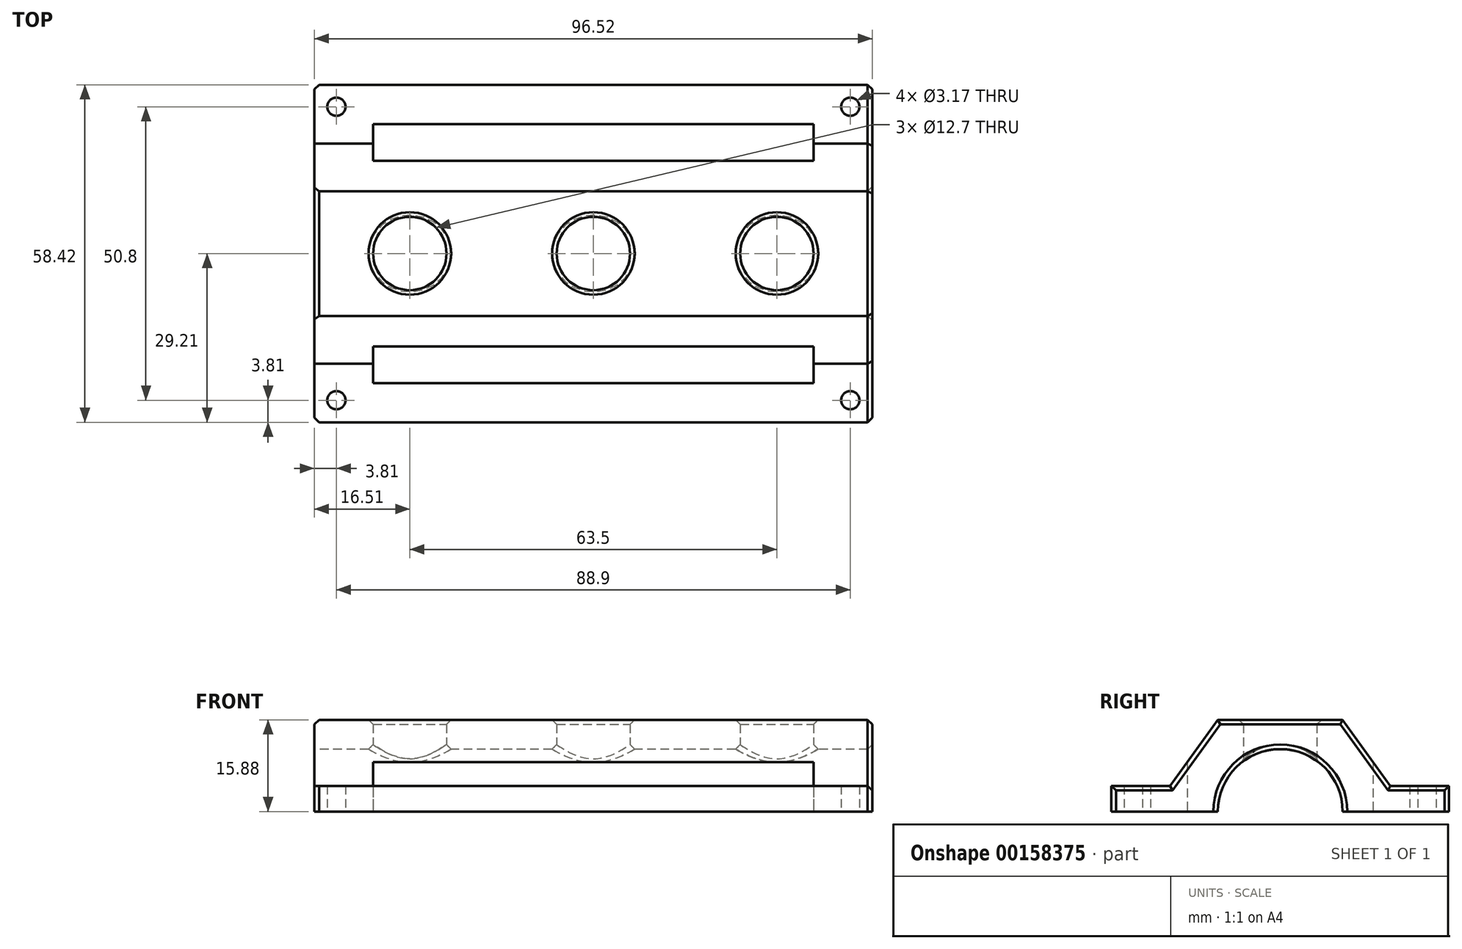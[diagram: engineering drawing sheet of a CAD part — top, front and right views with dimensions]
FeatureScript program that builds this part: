
annotation { "Feature Type Name" : "Feature", "Feature Type Description" : "" }
export const myFeature = defineFeature(function(context is Context, id is Id, definition is map)
    precondition{}
    {
        {
            var Q0;
            Q0=qCreatedBy(makeId("Top.planeOp"),FACE);
            var sketch = newSketch(context, id + "F0", { "sketchPlane" : qUnion([Q0])});
            skLineSegment(sketch, "E0", {"start": v(0, 0) * mm, "end": v(-48.26, 0) * mm});
            skLineSegment(sketch, "E1", {"start": v(-48.26, 0) * mm, "end": v(-48.26, 29.21) * mm});
            skLineSegment(sketch, "E2", {"start": v(-48.26, 29.21) * mm, "end": v(0, 29.21) * mm});
            skLineSegment(sketch, "E3", {"start": v(0, 29.21) * mm, "end": v(0, 0) * mm});
            skLineSegment(sketch, "E4.MirrorCS", {"start": v(48.26, 29.21) * mm, "end": v(0, 29.21) * mm});
            skLineSegment(sketch, "E5.MirrorCS", {"start": v(48.26, 0) * mm, "end": v(48.26, 29.21) * mm});
            skLineSegment(sketch, "E6.MirrorCS", {"start": v(0, 0) * mm, "end": v(48.26, 0) * mm});
            skLineSegment(sketch, "E7.MirrorCS", {"start": v(-48.26, -29.21) * mm, "end": v(0, -29.21) * mm});
            skLineSegment(sketch, "E8.MirrorCS", {"start": v(48.26, -29.2) * mm, "end": v(0, -29.21) * mm});
            skLineSegment(sketch, "E9.MirrorCS", {"start": v(48.26, 0) * mm, "end": v(48.26, -29.21) * mm});
            skLineSegment(sketch, "E10.MirrorCS", {"start": v(-48.26, 0) * mm, "end": v(-48.26, -29.21) * mm});
            skSolve(sketch);
        }
        {
            var Q0;
            Q0 = qSketchRegion(id + "F0", true);
            var Q1;
            Q1 = qSketchRegion(id + "F1MxHlLQY0lKD1c_1", true);
            extrude(context, id + "F1", {"entities" : qUnion([Q0, Q1]), "depth" : 15.88 * mm});
        }
        {
            var Q0;
            Q0=makeQuery(id+"F1.opExtrude","SWEPT_FACE",FACE,{"disambiguationData":[OSD([sQuery(id+"F0.wireOp",EDGE,"E1"),sQuery(id+"F0.wireOp",EDGE,"E10.MirrorCS")])]});
            var sketch = newSketch(context, id + "F2", { "sketchPlane" : qUnion([Q0])});
            skCircle(sketch, "E11", {"center": v(0, 0) * mm, "radius": 10.8 * mm});
            skLineSegment(sketch, "E12", {"start": v(-29.21, 15.88) * mm, "end": v(-10.8, 15.88) * mm});
            skLineSegment(sketch, "E13", {"start": v(-10.8, 15.88) * mm, "end": v(-19.05, 4.45) * mm});
            skLineSegment(sketch, "E14", {"start": v(-19.05, 4.45) * mm, "end": v(-29.21, 4.44) * mm});
            skLineSegment(sketch, "E15", {"start": v(-29.21, 4.44) * mm, "end": v(-29.21, 15.88) * mm});
            skLineSegment(sketch, "E16.MirrorCS", {"start": v(10.8, 15.88) * mm, "end": v(19.05, 4.44) * mm});
            skLineSegment(sketch, "E17.MirrorCS", {"start": v(19.05, 4.45) * mm, "end": v(29.21, 4.44) * mm});
            skLineSegment(sketch, "E18.MirrorCS", {"start": v(29.21, 4.44) * mm, "end": v(29.21, 15.88) * mm});
            skLineSegment(sketch, "E19.MirrorCS", {"start": v(29.21, 15.88) * mm, "end": v(10.8, 15.88) * mm});
            skSolve(sketch);
        }
        {
            var Q0;
            Q0 = qSketchRegion(id + "F2", true);
            extrude(context, id + "F3", {"entities" : qUnion([Q0]), "operationType" : NewBodyOperationType.REMOVE, "oppositeDirection" : true, "depth" : 101.6 * mm});
        }
        {
            var Q0;
            Q0=qCreatedBy(makeId("Top.planeOp"),FACE);
            var sketch = newSketch(context, id + "F4", { "sketchPlane" : qUnion([Q0])});
            skCircle(sketch, "E20", {"center": v(-44.45, 25.4) * mm, "radius": 1.59 * mm});
            skCircle(sketch, "E21.MirrorC", {"center": v(44.45, 25.4) * mm, "radius": 1.59 * mm});
            skCircle(sketch, "E22.MirrorC", {"center": v(44.45, -25.4) * mm, "radius": 1.59 * mm});
            skCircle(sketch, "E23.MirrorC", {"center": v(-44.45, -25.4) * mm, "radius": 1.59 * mm});
            skLineSegment(sketch, "E24.bottom", {"start": v(-38.1, 22.42) * mm, "end": v(38.1, 22.42) * mm});
            skLineSegment(sketch, "E24.top", {"start": v(-38.1, 16.07) * mm, "end": v(38.1, 16.07) * mm});
            skLineSegment(sketch, "E24.left", {"start": v(-38.1, 22.42) * mm, "end": v(-38.1, 16.07) * mm});
            skLineSegment(sketch, "E24.right", {"start": v(38.1, 22.42) * mm, "end": v(38.1, 16.07) * mm});
            skLineSegment(sketch, "E25.MirrorCS", {"start": v(-38.1, -16.07) * mm, "end": v(38.1, -16.07) * mm});
            skLineSegment(sketch, "E26.MirrorCS", {"start": v(-38.1, -22.42) * mm, "end": v(-38.1, -16.07) * mm});
            skLineSegment(sketch, "E27.MirrorCS", {"start": v(-38.1, -22.42) * mm, "end": v(38.1, -22.42) * mm});
            skLineSegment(sketch, "E28.MirrorCS", {"start": v(38.1, -22.42) * mm, "end": v(38.1, -16.07) * mm});
            skCircle(sketch, "E29", {"center": v(-31.75, 0) * mm, "radius": 6.35 * mm});
            skCircle(sketch, "E30", {"center": v(0, 0) * mm, "radius": 6.35 * mm});
            skCircle(sketch, "E31.MirrorC", {"center": v(31.75, 0) * mm, "radius": 6.35 * mm});
            skSolve(sketch);
        }
        {
            var Q0;
            Q0 = qSketchRegion(id + "F4", true);
            extrude(context, id + "F5", {"entities" : qUnion([Q0]), "operationType" : NewBodyOperationType.REMOVE, "depth" : 25.4 * mm});
        }
        {
            var Q0;
            Q0=makeQuery(id+"F5.boolean.opBoolean","COPY",EDGE,{"derivedFrom":makeQuery(id+"F5.opExtrude","CAP_EDGE",EDGE,{"disambiguationData":[OSD([sQuery(id+"F4.wireOp",EDGE,"E24.bottom")])],"isStart":true})});
            var Q1;
            Q1=makeQuery(id+"F5.boolean.opBoolean","COPY",EDGE,{"derivedFrom":makeQuery(id+"F5.opExtrude","CAP_EDGE",EDGE,{"disambiguationData":[OSD([sQuery(id+"F4.wireOp",EDGE,"E24.top")])],"isStart":true})});
            var Q2;
            Q2=makeQuery(id+"F5.boolean.opBoolean","COPY",EDGE,{"derivedFrom":makeQuery(id+"F5.opExtrude","CAP_EDGE",EDGE,{"disambiguationData":[OSD([sQuery(id+"F4.wireOp",EDGE,"E24.left")])],"isStart":true})});
            var Q3;
            Q3=makeQuery(id+"F5.boolean.opBoolean","COPY",EDGE,{"derivedFrom":makeQuery(id+"F5.opExtrude","CAP_EDGE",EDGE,{"disambiguationData":[OSD([sQuery(id+"F4.wireOp",EDGE,"E24.right")])],"isStart":true})});
            var Q4;
            Q4=makeQuery(id+"F5.boolean.opBoolean","COPY",EDGE,{"derivedFrom":makeQuery(id+"F5.opExtrude","CAP_EDGE",EDGE,{"disambiguationData":[OSD([sQuery(id+"F4.wireOp",EDGE,"E25.MirrorCS")])],"isStart":true})});
            var Q5;
            Q5=makeQuery(id+"F5.boolean.opBoolean","COPY",EDGE,{"derivedFrom":makeQuery(id+"F5.opExtrude","CAP_EDGE",EDGE,{"disambiguationData":[OSD([sQuery(id+"F4.wireOp",EDGE,"E27.MirrorCS")])],"isStart":true})});
            var Q6;
            Q6=makeQuery(id+"F5.boolean.opBoolean","COPY",EDGE,{"derivedFrom":makeQuery(id+"F5.opExtrude","CAP_EDGE",EDGE,{"disambiguationData":[OSD([sQuery(id+"F4.wireOp",EDGE,"E28.MirrorCS")])],"isStart":true})});
            var Q7;
            Q7=makeQuery(id+"F5.boolean.opBoolean","COPY",EDGE,{"derivedFrom":makeQuery(id+"F5.opExtrude","CAP_EDGE",EDGE,{"disambiguationData":[OSD([sQuery(id+"F4.wireOp",EDGE,"E26.MirrorCS")])],"isStart":true})});
            var Q8;
            Q8=makeQuery(id+"F5.boolean.opBoolean","INTERSECT",EDGE,{"derivedFrom":[makeQuery(id+"F3.boolean.opBoolean","COPY",FACE,{"derivedFrom":makeQuery(id+"F3.opExtrude","SWEPT_FACE",FACE,{"disambiguationData":[OSD([sQuery(id+"F2.wireOp",EDGE,"E11")])]})}),makeQuery(id+"F5.opExtrude","SWEPT_FACE",FACE,{"disambiguationData":[OSD([sQuery(id+"F4.wireOp",EDGE,"E29")])]})]});
            var Q9;
            Q9=makeQuery(id+"F5.boolean.opBoolean","INTERSECT",EDGE,{"derivedFrom":[makeQuery(id+"F3.boolean.opBoolean","COPY",FACE,{"derivedFrom":makeQuery(id+"F3.opExtrude","SWEPT_FACE",FACE,{"disambiguationData":[OSD([sQuery(id+"F2.wireOp",EDGE,"E11")])]})}),makeQuery(id+"F5.opExtrude","SWEPT_FACE",FACE,{"disambiguationData":[OSD([sQuery(id+"F4.wireOp",EDGE,"E30")])]})]});
            var Q10;
            Q10=makeQuery(id+"F5.boolean.opBoolean","INTERSECT",EDGE,{"derivedFrom":[makeQuery(id+"F3.boolean.opBoolean","COPY",FACE,{"derivedFrom":makeQuery(id+"F3.opExtrude","SWEPT_FACE",FACE,{"disambiguationData":[OSD([sQuery(id+"F2.wireOp",EDGE,"E11")])]})}),makeQuery(id+"F5.opExtrude","SWEPT_FACE",FACE,{"disambiguationData":[OSD([sQuery(id+"F4.wireOp",EDGE,"E31.MirrorC")])]})]});
            var Q11;
            Q11=makeQuery(id+"F5.boolean.opBoolean","INTERSECT",EDGE,{"derivedFrom":[makeQuery(id+"F1.opExtrude","CAP_FACE",FACE,{"disambiguationData":[OSD([sQuery(id+"F0.wireOp",EDGE,"E1"),sQuery(id+"F0.wireOp",EDGE,"E2"),sQuery(id+"F0.wireOp",EDGE,"E4.MirrorCS"),sQuery(id+"F0.wireOp",EDGE,"E5.MirrorCS"),sQuery(id+"F0.wireOp",EDGE,"E7.MirrorCS"),sQuery(id+"F0.wireOp",EDGE,"E8.MirrorCS"),sQuery(id+"F0.wireOp",EDGE,"E9.MirrorCS"),sQuery(id+"F0.wireOp",EDGE,"E10.MirrorCS")])],"isStart":false}),makeQuery(id+"F5.opExtrude","SWEPT_FACE",FACE,{"disambiguationData":[OSD([sQuery(id+"F4.wireOp",EDGE,"E31.MirrorC")])]})]});
            var Q12;
            Q12=makeQuery(id+"F5.boolean.opBoolean","INTERSECT",EDGE,{"derivedFrom":[makeQuery(id+"F1.opExtrude","CAP_FACE",FACE,{"disambiguationData":[OSD([sQuery(id+"F0.wireOp",EDGE,"E1"),sQuery(id+"F0.wireOp",EDGE,"E2"),sQuery(id+"F0.wireOp",EDGE,"E4.MirrorCS"),sQuery(id+"F0.wireOp",EDGE,"E5.MirrorCS"),sQuery(id+"F0.wireOp",EDGE,"E7.MirrorCS"),sQuery(id+"F0.wireOp",EDGE,"E8.MirrorCS"),sQuery(id+"F0.wireOp",EDGE,"E9.MirrorCS"),sQuery(id+"F0.wireOp",EDGE,"E10.MirrorCS")])],"isStart":false}),makeQuery(id+"F5.opExtrude","SWEPT_FACE",FACE,{"disambiguationData":[OSD([sQuery(id+"F4.wireOp",EDGE,"E30")])]})]});
            var Q13;
            Q13=makeQuery(id+"F5.boolean.opBoolean","INTERSECT",EDGE,{"derivedFrom":[makeQuery(id+"F1.opExtrude","CAP_FACE",FACE,{"disambiguationData":[OSD([sQuery(id+"F0.wireOp",EDGE,"E1"),sQuery(id+"F0.wireOp",EDGE,"E2"),sQuery(id+"F0.wireOp",EDGE,"E4.MirrorCS"),sQuery(id+"F0.wireOp",EDGE,"E5.MirrorCS"),sQuery(id+"F0.wireOp",EDGE,"E7.MirrorCS"),sQuery(id+"F0.wireOp",EDGE,"E8.MirrorCS"),sQuery(id+"F0.wireOp",EDGE,"E9.MirrorCS"),sQuery(id+"F0.wireOp",EDGE,"E10.MirrorCS")])],"isStart":false}),makeQuery(id+"F5.opExtrude","SWEPT_FACE",FACE,{"disambiguationData":[OSD([sQuery(id+"F4.wireOp",EDGE,"E29")])]})]});
            var Q14;
            Q14=makeQuery(id+"F3.boolean.opBoolean","INTERSECT",EDGE,{"derivedFrom":[makeQuery(id+"F1.opExtrude","SWEPT_FACE",FACE,{"disambiguationData":[OSD([sQuery(id+"F0.wireOp",EDGE,"E5.MirrorCS"),sQuery(id+"F0.wireOp",EDGE,"E9.MirrorCS")])]}),makeQuery(id+"F3.opExtrude","SWEPT_FACE",FACE,{"disambiguationData":[OSD([sQuery(id+"F2.wireOp",EDGE,"E11")])]})]});
            var Q15;
            Q15=makeQuery(id+"F3.boolean.opBoolean","COPY",EDGE,{"derivedFrom":makeQuery(id+"F3.opExtrude","CAP_EDGE",EDGE,{"disambiguationData":[OSD([sQuery(id+"F2.wireOp",EDGE,"E11")])],"isStart":true})});
            var Q16;
            Q16=makeQuery(id+"F3.boolean.opBoolean","COPY",EDGE,{"derivedFrom":makeQuery(id+"F3.opExtrude","CAP_EDGE",EDGE,{"disambiguationData":[OSD([sQuery(id+"F2.wireOp",EDGE,"E16.MirrorCS")])],"isStart":true})});
            var Q17;
            Q17=makeQuery(id+"F3.boolean.opBoolean","COPY",EDGE,{"derivedFrom":makeQuery(id+"F3.opExtrude","CAP_EDGE",EDGE,{"disambiguationData":[OSD([sQuery(id+"F2.wireOp",EDGE,"E17.MirrorCS")])],"isStart":true})});
            var Q18;
            Q18=makeQuery(id+"F1.opExtrude","CAP_EDGE",EDGE,{"disambiguationData":[OSD([sQuery(id+"F0.wireOp",EDGE,"E1"),sQuery(id+"F0.wireOp",EDGE,"E10.MirrorCS")])],"isStart":false});
            var Q19;
            Q19=makeQuery(id+"F3.boolean.opBoolean","COPY",EDGE,{"derivedFrom":makeQuery(id+"F3.opExtrude","CAP_EDGE",EDGE,{"disambiguationData":[OSD([sQuery(id+"F2.wireOp",EDGE,"E13")])],"isStart":true})});
            var Q20;
            Q20=makeQuery(id+"F3.boolean.opBoolean","COPY",EDGE,{"derivedFrom":makeQuery(id+"F3.opExtrude","CAP_EDGE",EDGE,{"disambiguationData":[OSD([sQuery(id+"F2.wireOp",EDGE,"E14")])],"isStart":true})});
            var Q21;
            Q21=makeQuery(id+"F3.boolean.opBoolean","COPY",EDGE,{"derivedFrom":makeQuery(id+"F3.opExtrude","SWEPT_EDGE",EDGE,{"disambiguationData":[OSD([sQuery(id+"F0.wireOp",EDGE,"E1"),sQuery(id+"F0.wireOp",EDGE,"E2"),sQuery(id+"F2.wireOp",EDGE,"E14"),sQuery(id+"F2.wireOp",EDGE,"E15")])]})});
            var Q22;
            Q22=makeQuery(id+"F3.boolean.opBoolean","INTERSECT",EDGE,{"derivedFrom":[makeQuery(id+"F1.opExtrude","SWEPT_FACE",FACE,{"disambiguationData":[OSD([sQuery(id+"F0.wireOp",EDGE,"E5.MirrorCS"),sQuery(id+"F0.wireOp",EDGE,"E9.MirrorCS")])]}),makeQuery(id+"F3.opExtrude","SWEPT_FACE",FACE,{"disambiguationData":[OSD([sQuery(id+"F2.wireOp",EDGE,"E14")])]})]});
            var Q23;
            Q23=makeQuery(id+"F1.opExtrude","CAP_EDGE",EDGE,{"disambiguationData":[OSD([sQuery(id+"F0.wireOp",EDGE,"E5.MirrorCS"),sQuery(id+"F0.wireOp",EDGE,"E9.MirrorCS")])],"isStart":false});
            var Q24;
            Q24=makeQuery(id+"F3.boolean.opBoolean","INTERSECT",EDGE,{"derivedFrom":[makeQuery(id+"F1.opExtrude","SWEPT_FACE",FACE,{"disambiguationData":[OSD([sQuery(id+"F0.wireOp",EDGE,"E5.MirrorCS"),sQuery(id+"F0.wireOp",EDGE,"E9.MirrorCS")])]}),makeQuery(id+"F3.opExtrude","SWEPT_FACE",FACE,{"disambiguationData":[OSD([sQuery(id+"F2.wireOp",EDGE,"E16.MirrorCS")])]})]});
            var Q25;
            Q25=makeQuery(id+"F3.boolean.opBoolean","INTERSECT",EDGE,{"derivedFrom":[makeQuery(id+"F1.opExtrude","SWEPT_FACE",FACE,{"disambiguationData":[OSD([sQuery(id+"F0.wireOp",EDGE,"E5.MirrorCS"),sQuery(id+"F0.wireOp",EDGE,"E9.MirrorCS")])]}),makeQuery(id+"F3.opExtrude","SWEPT_FACE",FACE,{"disambiguationData":[OSD([sQuery(id+"F2.wireOp",EDGE,"E17.MirrorCS")])]})]});
            var Q26;
            Q26=makeQuery(id+"F3.boolean.opBoolean","COPY",EDGE,{"derivedFrom":makeQuery(id+"F3.opExtrude","SWEPT_EDGE",EDGE,{"disambiguationData":[OSD([sQuery(id+"F0.wireOp",EDGE,"E7.MirrorCS"),sQuery(id+"F0.wireOp",EDGE,"E10.MirrorCS"),sQuery(id+"F2.wireOp",EDGE,"E17.MirrorCS"),sQuery(id+"F2.wireOp",EDGE,"E18.MirrorCS")])]})});
            var Q27;
            Q27=makeQuery(id+"F3.boolean.opBoolean","INTERSECT",EDGE,{"derivedFrom":[makeQuery(id+"F1.opExtrude","SWEPT_FACE",FACE,{"disambiguationData":[OSD([sQuery(id+"F0.wireOp",EDGE,"E5.MirrorCS"),sQuery(id+"F0.wireOp",EDGE,"E9.MirrorCS")])]}),makeQuery(id+"F3.opExtrude","SWEPT_FACE",FACE,{"disambiguationData":[OSD([sQuery(id+"F2.wireOp",EDGE,"E13")])]})]});
            var Q28;
            Q28=makeQuery(id+"F1.opExtrude","SWEPT_EDGE",EDGE,{"disambiguationData":[OSD([sQuery(id+"F0.wireOp",EDGE,"E7.MirrorCS"),sQuery(id+"F0.wireOp",EDGE,"E10.MirrorCS")])]});
            var Q29;
            Q29=makeQuery(id+"F1.opExtrude","SWEPT_EDGE",EDGE,{"disambiguationData":[OSD([sQuery(id+"F0.wireOp",EDGE,"E1"),sQuery(id+"F0.wireOp",EDGE,"E2")])]});
            var Q30;
            Q30=makeQuery(id+"F1.opExtrude","SWEPT_EDGE",EDGE,{"disambiguationData":[OSD([sQuery(id+"F0.wireOp",EDGE,"E4.MirrorCS"),sQuery(id+"F0.wireOp",EDGE,"E5.MirrorCS")])]});
            var Q31;
            Q31=makeQuery(id+"F1.opExtrude","SWEPT_EDGE",EDGE,{"disambiguationData":[OSD([sQuery(id+"F0.wireOp",EDGE,"E8.MirrorCS"),sQuery(id+"F0.wireOp",EDGE,"E9.MirrorCS")])]});
            var Q32;
            Q32=makeQuery(id+"F3.boolean.opBoolean","COPY",EDGE,{"derivedFrom":makeQuery(id+"F3.opExtrude","SWEPT_EDGE",EDGE,{"disambiguationData":[OSD([sQuery(id+"F0.wireOp",EDGE,"E1"),sQuery(id+"F0.wireOp",EDGE,"E10.MirrorCS"),sQuery(id+"F2.wireOp",EDGE,"E12"),sQuery(id+"F2.wireOp",EDGE,"E13")])]})});
            var Q33;
            Q33=makeQuery(id+"F3.boolean.opBoolean","COPY",EDGE,{"derivedFrom":makeQuery(id+"F3.opExtrude","SWEPT_EDGE",EDGE,{"disambiguationData":[OSD([sQuery(id+"F0.wireOp",EDGE,"E1"),sQuery(id+"F0.wireOp",EDGE,"E10.MirrorCS"),sQuery(id+"F2.wireOp",EDGE,"E16.MirrorCS"),sQuery(id+"F2.wireOp",EDGE,"E19.MirrorCS")])]})});
            chamfer(context, id + "F6", {"entities" : qUnion([Q0, Q1, Q2, Q3, Q4, Q5, Q6, Q7, Q8, Q9, Q10, Q11, Q12, Q13, Q14, Q15, Q16, Q17, Q18, Q19, Q20, Q21, Q22, Q23, Q24, Q25, Q26, Q27, Q28, Q29, Q30, Q31, Q32, Q33]), "width" : 0.8 * mm, "tangentPropagation" : true});
        }
    });
